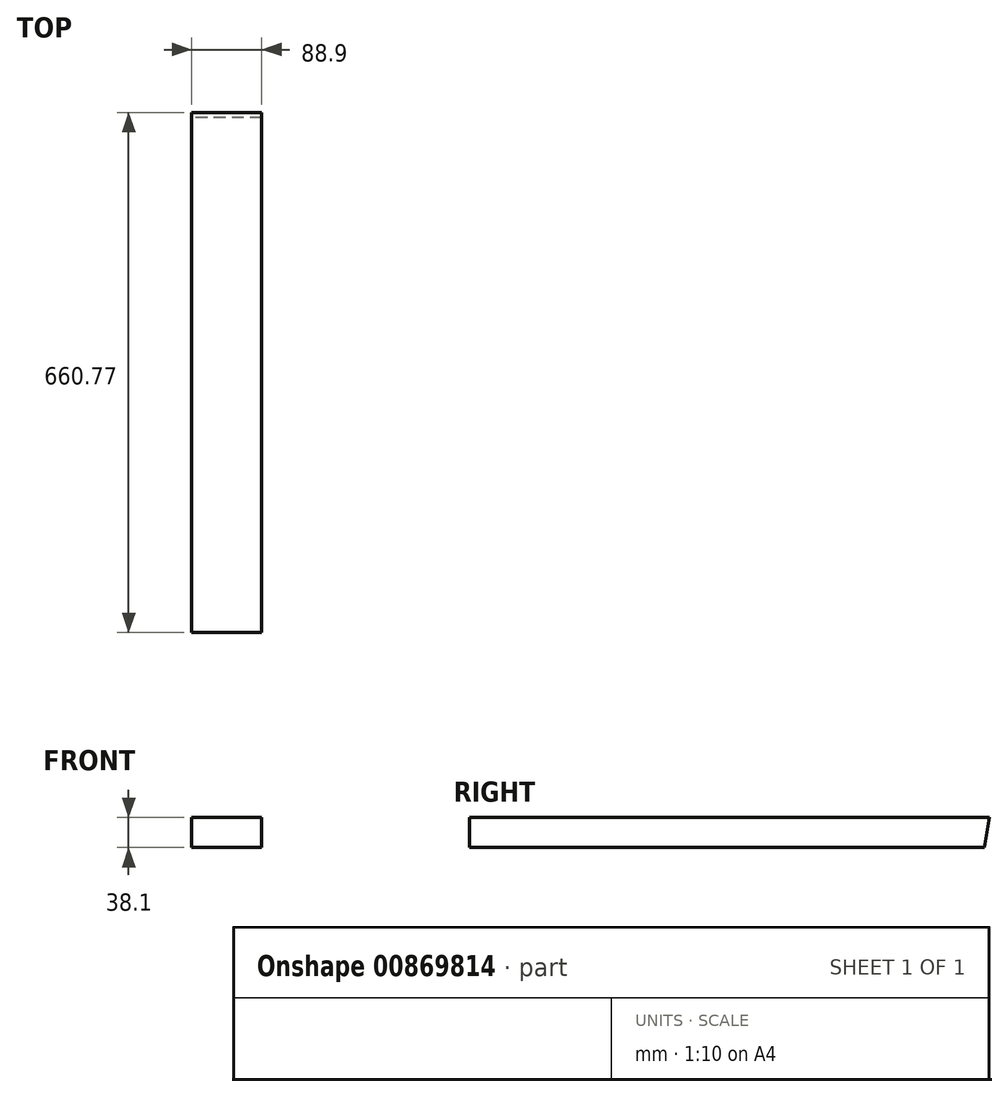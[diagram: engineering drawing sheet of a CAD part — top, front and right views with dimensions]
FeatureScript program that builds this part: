
annotation { "Feature Type Name" : "Feature", "Feature Type Description" : "" }
export const myFeature = defineFeature(function(context is Context, id is Id, definition is map)
    precondition{}
    {
        {
            var Q0;
            Q0=qCreatedBy(makeId("Front.planeOp"),FACE);
            var sketch = newSketch(context, id + "F0", { "sketchPlane" : qUnion([Q0])});
            skLineSegment(sketch, "E0.bottom", {"start": v(44.45, -19.05) * mm, "end": v(-44.45, -19.05) * mm});
            skLineSegment(sketch, "E0.top", {"start": v(44.45, 19.05) * mm, "end": v(-44.45, 19.05) * mm});
            skLineSegment(sketch, "E0.left", {"start": v(44.45, -19.05) * mm, "end": v(44.45, 19.05) * mm});
            skLineSegment(sketch, "E0.right", {"start": v(-44.45, -19.05) * mm, "end": v(-44.45, 19.05) * mm});
            skPoint(sketch, "E0.middle", {"position": v(0, 0) * mm});
            skSolve(sketch);
        }
        {
            var Q0;
            Q0=makeQuery(id+"F0.imprint","IMPRINT",FACE,{"disambiguationData":[TD([[makeQuery(id+"F0.imprint","IMPRINT",EDGE,{"derivedFrom":sQuery(id+"F0.wireOp",EDGE,"E0.bottom")}),-1.0]])]});
            extrude(context, id + "F1", {"entities" : qUnion([Q0]), "oppositeDirection" : true, "depth" : 654.05 * mm, "offsetDistance" : 25.4 * mm});
        }
        {
            var Q0;
            Q0=makeQuery(id+"F1.opExtrude","SWEPT_FACE",FACE,{"disambiguationData":[OSD([sQuery(id+"F0.wireOp",EDGE,"E0.left")])]});
            var sketch = newSketch(context, id + "F2", { "sketchPlane" : qUnion([Q0])});
            skLineSegment(sketch, "E1", {"start": v(654.05, -19.05) * mm, "end": v(660.77, 19.05) * mm});
            skLineSegment(sketch, "E2", {"start": v(660.77, 19.05) * mm, "end": v(654.05, 19.05) * mm});
            skLineSegment(sketch, "E3", {"start": v(654.05, 19.05) * mm, "end": v(654.05, -19.05) * mm});
            skSolve(sketch);
        }
        {
            var Q0;
            Q0 = qSketchRegion(id + "F2", true);
            extrude(context, id + "F3", {"entities" : qUnion([Q0]), "operationType" : NewBodyOperationType.ADD, "oppositeDirection" : true, "depth" : 88.9 * mm, "offsetDistance" : 25.4 * mm});
        }
    });
